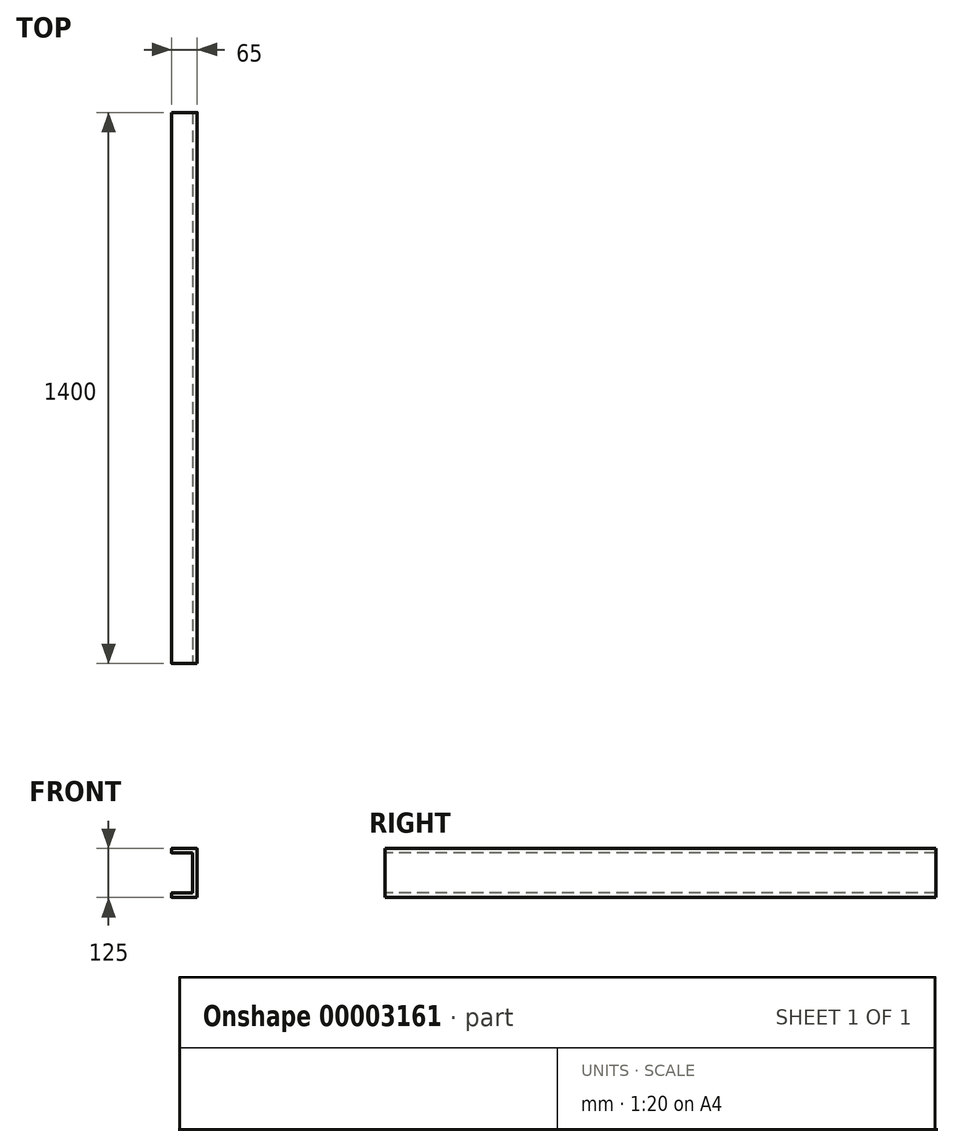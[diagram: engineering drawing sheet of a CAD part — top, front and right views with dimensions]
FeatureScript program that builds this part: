
annotation { "Feature Type Name" : "Feature", "Feature Type Description" : "" }
export const myFeature = defineFeature(function(context is Context, id is Id, definition is map)
    precondition{}
    {
        {
            var Q0;
            Q0=qCreatedBy(makeId("Front.planeOp"),FACE);
            var sketch = newSketch(context, id + "F0", { "sketchPlane" : qUnion([Q0])});
            skLineSegment(sketch, "E0.bottom", {"start": v(-0.5, 125) * mm, "end": v(-64.5, 125) * mm});
            skLineSegment(sketch, "E0.top", {"start": v(0, 0) * mm, "end": v(-64.5, 0) * mm});
            skLineSegment(sketch, "E0.left", {"start": v(0, 124.5) * mm, "end": v(0, 0) * mm});
            skLineSegment(sketch, "E1.bottom", {"start": v(-64.5, 12) * mm, "end": v(-12.5, 12) * mm});
            skLineSegment(sketch, "E1.top", {"start": v(-64.5, 113) * mm, "end": v(-12.5, 113) * mm});
            skLineSegment(sketch, "E1.right", {"start": v(-12, 12.5) * mm, "end": v(-12, 112.5) * mm});
            skPoint(sketch, "E2", {"position": v(-65, 113) * mm});
            skLineSegment(sketch, "E3", {"start": v(-65, 11.5) * mm, "end": v(-65, 0.5) * mm});
            skLineSegment(sketch, "E4", {"start": v(-65, 113.5) * mm, "end": v(-65, 124.5) * mm});
            skPoint(sketch, "E5.visualSharp", {"position": v(-65, 125) * mm});
            skArc(sketch, "E5.filletArc", {"start": v(-64.5, 125) * mm, "mid": v(-64.85, 124.85) * mm, "end": v(-65, 124.5) * mm});
            skArc(sketch, "E6.filletArc", {"start": v(-65, 113.5) * mm, "mid": v(-64.85, 113.15) * mm, "end": v(-64.5, 113) * mm});
            skPoint(sketch, "E7.visualSharp", {"position": v(-65, 12) * mm});
            skArc(sketch, "E7.filletArc", {"start": v(-64.5, 12) * mm, "mid": v(-64.85, 11.85) * mm, "end": v(-65, 11.5) * mm});
            skPoint(sketch, "E8.visualSharp", {"position": v(-65, 0) * mm});
            skArc(sketch, "E8.filletArc", {"start": v(-65, 0.5) * mm, "mid": v(-64.85, 0.15) * mm, "end": v(-64.5, 0) * mm});
            skPoint(sketch, "E9.visualSharp", {"position": v(-12, 12) * mm});
            skArc(sketch, "E9.filletArc", {"start": v(-12.5, 12) * mm, "mid": v(-12.15, 12.15) * mm, "end": v(-12, 12.5) * mm});
            skPoint(sketch, "E10.visualSharp", {"position": v(0, 0) * mm});
            skPoint(sketch, "E11.visualSharp", {"position": v(-12, 113) * mm});
            skArc(sketch, "E11.filletArc", {"start": v(-12, 112.5) * mm, "mid": v(-12.15, 112.85) * mm, "end": v(-12.5, 113) * mm});
            skPoint(sketch, "E12.visualSharp", {"position": v(0, 125) * mm});
            skArc(sketch, "E12.filletArc", {"start": v(0, 124.5) * mm, "mid": v(-0.15, 124.85) * mm, "end": v(-0.5, 125) * mm});
            skLineSegment(sketch, "E13", {"start": v(-65, 113) * mm, "end": v(-65, 12) * mm});
            skPoint(sketch, "E14", {"position": v(-57, 119) * mm});
            skPoint(sketch, "E15", {"position": v(-40, 119) * mm});
            skPoint(sketch, "E16", {"position": v(-6, 119) * mm});
            skPoint(sketch, "E17", {"position": v(-23, 119) * mm});
            skLineSegment(sketch, "E18", {"start": v(-57, 119) * mm, "end": v(-40, 119) * mm, "construction": true});
            skLineSegment(sketch, "E19", {"start": v(-40, 119) * mm, "end": v(-23, 119) * mm, "construction": true});
            skLineSegment(sketch, "E20", {"start": v(-23, 119) * mm, "end": v(-6, 119) * mm, "construction": true});
            skLineSegment(sketch, "E21", {"start": v(-6, 6) * mm, "end": v(-23, 6) * mm, "construction": true});
            skLineSegment(sketch, "E22", {"start": v(-23, 6) * mm, "end": v(-40, 6) * mm, "construction": true});
            skLineSegment(sketch, "E23", {"start": v(-40, 6) * mm, "end": v(-57, 6) * mm, "construction": true});
            skLineSegment(sketch, "E24", {"start": v(-6, 119) * mm, "end": v(-6, 100.17) * mm, "construction": true});
            skLineSegment(sketch, "E25", {"start": v(-6, 100.17) * mm, "end": v(-6, 81.33) * mm, "construction": true});
            skLineSegment(sketch, "E26", {"start": v(-6, 81.33) * mm, "end": v(-6, 62.5) * mm, "construction": true});
            skLineSegment(sketch, "E27", {"start": v(-6, 62.5) * mm, "end": v(-6, 43.67) * mm, "construction": true});
            skLineSegment(sketch, "E28", {"start": v(-6, 43.67) * mm, "end": v(-6, 24.83) * mm, "construction": true});
            skLineSegment(sketch, "E29", {"start": v(-6, 24.83) * mm, "end": v(-6, 6) * mm, "construction": true});
            skPoint(sketch, "E30", {"position": v(-6, 100.17) * mm});
            skPoint(sketch, "E31", {"position": v(-6, 81.33) * mm});
            skPoint(sketch, "E32", {"position": v(-6, 62.5) * mm});
            skPoint(sketch, "E33", {"position": v(-6, 43.67) * mm});
            skPoint(sketch, "E34", {"position": v(-6, 24.83) * mm});
            skPoint(sketch, "E35", {"position": v(-6, 6) * mm});
            skPoint(sketch, "E36", {"position": v(-23, 6) * mm});
            skPoint(sketch, "E37", {"position": v(-40, 6) * mm});
            skPoint(sketch, "E38", {"position": v(-57, 6) * mm});
            skSolve(sketch);
        }
        {
            var Q0;
            Q0=makeQuery(id+"F0.imprint","IMPRINT",FACE,{"disambiguationData":[TD([[makeQuery(id+"F0.imprint","IMPRINT",EDGE,{"derivedFrom":sQuery(id+"F0.wireOp",EDGE,"E0.bottom")}),1.0]])]});
            extrude(context, id + "F1", {"entities" : qUnion([Q0]), "flatOperationType" : FlatOperationType.REMOVE, "oppositeDirection" : true, "offsetDistance" : 25 * mm, "depth" : 1400 * mm, "domain" : OperationDomain.MODEL, "symmetric" : true});
        }
    });
